FCSTD DOCUMENT
Label: Full set of dividers
objects: Sketcher::SketchObject×14
note: 14 computed .brp shape members not serialized (recipe doc carries the construction recipe); baked Part::Feature solids carry a one-line shape summary decoded from their .brp

FEATURE [Sketcher::SketchObject] Sketch  label="divider A000"
  sketch-geometry (20):
    g0: LineSegment StartX=0 StartY=31.25 StartZ=0 EndX=32 EndY=31.25 EndZ=0
    g1: LineSegment StartX=32 StartY=31.25 StartZ=0 EndX=32 EndY=15.625 EndZ=0
    g2: LineSegment StartX=32 StartY=15.625 StartZ=0 EndX=35 EndY=15.625 EndZ=0
    g3: LineSegment StartX=35 StartY=15.625 StartZ=0 EndX=35 EndY=31.25 EndZ=0
    g4: LineSegment StartX=35 StartY=31.25 StartZ=0 EndX=64 EndY=31.25 EndZ=0
    g5: LineSegment StartX=64 StartY=31.25 StartZ=0 EndX=64 EndY=15.625 EndZ=0
    g6: LineSegment StartX=64 StartY=15.625 StartZ=0 EndX=67 EndY=15.625 EndZ=0
    g7: LineSegment StartX=67 StartY=15.625 StartZ=0 EndX=67 EndY=31.25 EndZ=0
    g8: LineSegment StartX=67 StartY=31.25 StartZ=0 EndX=96 EndY=31.25 EndZ=0
    g9: LineSegment StartX=96 StartY=31.25 StartZ=0 EndX=96 EndY=15.625 EndZ=0
    g10: LineSegment StartX=96 StartY=15.625 StartZ=0 EndX=99 EndY=15.625 EndZ=0
    g11: LineSegment StartX=99 StartY=15.625 StartZ=0 EndX=99 EndY=31.25 EndZ=0
    g12: LineSegment StartX=99 StartY=31.25 StartZ=0 EndX=131 EndY=31.25 EndZ=0
    g13: LineSegment StartX=131 StartY=31.25 StartZ=0 EndX=131 EndY=15.625 EndZ=0
    g14: LineSegment StartX=131 StartY=15.625 StartZ=0 EndX=128 EndY=15.625 EndZ=0
    g15: LineSegment StartX=128 StartY=15.625 StartZ=0 EndX=128 EndY=0 EndZ=0
    g16: LineSegment StartX=128 StartY=0 StartZ=0 EndX=3 EndY=0 EndZ=0
    g17: LineSegment StartX=3 StartY=0 StartZ=0 EndX=3 EndY=15.625 EndZ=0
    g18: LineSegment StartX=3 StartY=15.625 StartZ=0 EndX=0 EndY=15.625 EndZ=0
    g19: LineSegment StartX=0 StartY=15.625 StartZ=0 EndX=0 EndY=31.25 EndZ=0
  constraints (60):
    c: Horizontal(g0)
    c: Coincident(g0,g1)
    c: Vertical(g1)
    c: Coincident(g1,g2)
    c: Horizontal(g2)
    c: Coincident(g2,g3)
    c: Coincident(g3,g4)
    c: Horizontal(g4)
    c: Coincident(g4,g5)
    c: Coincident(g5,g6)
    c: Horizontal(g6)
    c: Coincident(g6,g7)
    c: Coincident(g7,g8)
    c: Coincident(g8,g9)
    c: Vertical(g9)
    c: Coincident(g9,g10)
    c: Coincident(g10,g11)
    c: Vertical(g11)
    c: Coincident(g11,g12)
    c: Horizontal(g12)
    c: Coincident(g12,g13)
    c: Vertical(g13)
    c: Coincident(g13,g14)
    c: Coincident(g14,g15)
    c: Vertical(g15)
    c: Coincident(g15,g16)
    c: Horizontal(g16)
    c: Coincident(g16,g17)
    c: Vertical(g17)
    c: Coincident(g17,g18)
    c: Coincident(g18,g19)
    c: Coincident(g19,g0)
    c: Horizontal(g10)
    c: Horizontal(g14)
    c: Horizontal(g18)
    c: Vertical(g19)
    c: Vertical(g3)
    c: Vertical(g5)
    c: Vertical(g7)
    c: Horizontal(g8)
    c: DistanceY(g0,g3) = 0
    c: DistanceY(g4,g7) = 0
    c: DistanceY(g8,g11) = 0
    c: DistanceY(g6,g9) = 0
    c: DistanceY(g5,g2) = 0
    c: DistanceX(g1,g2) = 3
    c: DistanceX(g5,g6) = 3
    c: DistanceX(g8,g11) = 3
    c: DistanceY(g15,g12) = 31.25
    c: DistanceY(g13,g12) = 15.625
    c: DistanceY(g10,g14) = 0
    c: DistanceY(g17,g1) = 0
    c: DistanceX(g13,g14) = -3
    c: DistanceX(g18,g17) = 3
    c: DistanceX(g12,g11) = -32
    c: DistanceX(g4,g3) = -29
    c: DistanceX(g0,g0) = -32
    c: DistanceX(g7,g8) = 29
    c: DistanceX(g16) = 3
    c: DistanceY(g16) = 0
FEATURE [Sketcher::SketchObject] Sketch001  label="divider A001"
  Placement = pos=(0,62.5,0) rot=(1,0,0;3.14159rad)
  sketch-geometry (16):
    g0: LineSegment StartX=32 StartY=31.25 StartZ=0 EndX=32 EndY=15.625 EndZ=0
    g1: LineSegment StartX=32 StartY=15.625 StartZ=0 EndX=35 EndY=15.625 EndZ=0
    g2: LineSegment StartX=35 StartY=15.625 StartZ=0 EndX=35 EndY=31.25 EndZ=0
    g3: LineSegment StartX=64 StartY=31.25 StartZ=0 EndX=64 EndY=15.625 EndZ=0
    g4: LineSegment StartX=64 StartY=15.625 StartZ=0 EndX=67 EndY=15.625 EndZ=0
    g5: LineSegment StartX=67 StartY=15.625 StartZ=0 EndX=67 EndY=31.25 EndZ=0
    g6: LineSegment StartX=96 StartY=31.25 StartZ=0 EndX=96 EndY=15.625 EndZ=0
    g7: LineSegment StartX=96 StartY=15.625 StartZ=0 EndX=99 EndY=15.625 EndZ=0
    g8: LineSegment StartX=99 StartY=15.625 StartZ=0 EndX=99 EndY=31.25 EndZ=0
    g9: LineSegment StartX=131 StartY=31.25 StartZ=0 EndX=131 EndY=15.625 EndZ=0
    g10: LineSegment StartX=131 StartY=15.625 StartZ=0 EndX=128 EndY=15.625 EndZ=0
    g11: LineSegment StartX=128 StartY=15.625 StartZ=0 EndX=128 EndY=0 EndZ=0
    g12: LineSegment StartX=128 StartY=0 StartZ=0 EndX=3 EndY=0 EndZ=0
    g13: LineSegment StartX=3 StartY=0 StartZ=0 EndX=3 EndY=15.625 EndZ=0
    g14: LineSegment StartX=3 StartY=15.625 StartZ=0 EndX=0 EndY=15.625 EndZ=0
    g15: LineSegment StartX=0 StartY=15.625 StartZ=0 EndX=0 EndY=31.25 EndZ=0
  constraints (38):
    c: Vertical(g0)
    c: Coincident(g0,g1)
    c: Horizontal(g1)
    c: Coincident(g1,g2)
    c: Coincident(g3,g4)
    c: Horizontal(g4)
    c: Coincident(g4,g5)
    c: Vertical(g6)
    c: Coincident(g6,g7)
    c: Coincident(g7,g8)
    c: Vertical(g8)
    c: Vertical(g9)
    c: Coincident(g9,g10)
    c: Coincident(g10,g11)
    c: Vertical(g11)
    c: Coincident(g11,g12)
    c: Horizontal(g12)
    c: Coincident(g12,g13)
    c: Vertical(g13)
    c: Coincident(g13,g14)
    c: Coincident(g14,g15)
    c: Horizontal(g7)
    c: Horizontal(g10)
    c: Horizontal(g14)
    c: Vertical(g15)
    c: Vertical(g2)
    c: Vertical(g3)
    c: Vertical(g5)
    c: DistanceY(g4,g6) = 0
    c: DistanceY(g3,g1) = 0
    c: DistanceX(g0,g1) = 3
    c: DistanceX(g3,g4) = 3
    c: DistanceY(g7,g10) = 0
    c: DistanceY(g13,g0) = 0
    c: DistanceX(g9,g10) = -3
    c: DistanceX(g14,g13) = 3
    c: DistanceX(g12) = 3
    c: DistanceY(g12) = 0
FEATURE [Sketcher::SketchObject] Sketch002  label="divider A002"
  Placement = pos=(0,62.5,0) rot=(0,0,1;0rad)
  sketch-geometry (19):
    g0: LineSegment StartX=0 StartY=31.25 StartZ=0 EndX=32 EndY=31.25 EndZ=0
    g1: LineSegment StartX=32 StartY=31.25 StartZ=0 EndX=32 EndY=15.625 EndZ=0
    g2: LineSegment StartX=32 StartY=15.625 StartZ=0 EndX=35 EndY=15.625 EndZ=0
    g3: LineSegment StartX=35 StartY=15.625 StartZ=0 EndX=35 EndY=31.25 EndZ=0
    g4: LineSegment StartX=35 StartY=31.25 StartZ=0 EndX=64 EndY=31.25 EndZ=0
    g5: LineSegment StartX=64 StartY=31.25 StartZ=0 EndX=64 EndY=15.625 EndZ=0
    g6: LineSegment StartX=64 StartY=15.625 StartZ=0 EndX=67 EndY=15.625 EndZ=0
    g7: LineSegment StartX=67 StartY=15.625 StartZ=0 EndX=67 EndY=31.25 EndZ=0
    g8: LineSegment StartX=67 StartY=31.25 StartZ=0 EndX=96 EndY=31.25 EndZ=0
    g9: LineSegment StartX=96 StartY=31.25 StartZ=0 EndX=96 EndY=15.625 EndZ=0
    g10: LineSegment StartX=96 StartY=15.625 StartZ=0 EndX=99 EndY=15.625 EndZ=0
    g11: LineSegment StartX=99 StartY=15.625 StartZ=0 EndX=99 EndY=31.25 EndZ=0
    g12: LineSegment StartX=99 StartY=31.25 StartZ=0 EndX=131 EndY=31.25 EndZ=0
    g13: LineSegment StartX=131 StartY=31.25 StartZ=0 EndX=131 EndY=15.625 EndZ=0
    g14: LineSegment StartX=131 StartY=15.625 StartZ=0 EndX=128 EndY=15.625 EndZ=0
    g15: LineSegment StartX=128 StartY=15.625 StartZ=0 EndX=128 EndY=0 EndZ=0
    g16: LineSegment StartX=3 StartY=0 StartZ=0 EndX=3 EndY=15.625 EndZ=0
    g17: LineSegment StartX=3 StartY=15.625 StartZ=0 EndX=0 EndY=15.625 EndZ=0
    g18: LineSegment StartX=0 StartY=15.625 StartZ=0 EndX=0 EndY=31.25 EndZ=0
  constraints (55):
    c: Horizontal(g0)
    c: Coincident(g0,g1)
    c: Vertical(g1)
    c: Coincident(g1,g2)
    c: Horizontal(g2)
    c: Coincident(g2,g3)
    c: Coincident(g3,g4)
    c: Horizontal(g4)
    c: Coincident(g4,g5)
    c: Coincident(g5,g6)
    c: Horizontal(g6)
    c: Coincident(g6,g7)
    c: Coincident(g7,g8)
    c: Coincident(g8,g9)
    c: Vertical(g9)
    c: Coincident(g9,g10)
    c: Coincident(g10,g11)
    c: Vertical(g11)
    c: Coincident(g11,g12)
    c: Horizontal(g12)
    c: Coincident(g12,g13)
    c: Vertical(g13)
    c: Coincident(g13,g14)
    c: Coincident(g14,g15)
    c: Vertical(g15)
    c: Vertical(g16)
    c: Coincident(g16,g17)
    c: Coincident(g17,g18)
    c: Coincident(g18,g0)
    c: Horizontal(g10)
    c: Horizontal(g14)
    c: Horizontal(g17)
    c: Vertical(g18)
    c: Vertical(g3)
    c: Vertical(g5)
    c: Vertical(g7)
    c: Horizontal(g8)
    c: DistanceY(g0,g3) = 0
    c: DistanceY(g4,g7) = 0
    c: DistanceY(g8,g11) = 0
    c: DistanceY(g6,g9) = 0
    c: DistanceY(g5,g2) = 0
    c: DistanceX(g1,g2) = 3
    c: DistanceX(g5,g6) = 3
    c: DistanceX(g8,g11) = 3
    c: DistanceY(g15,g12) = 31.25
    c: DistanceY(g13,g12) = 15.625
    c: DistanceY(g10,g14) = 0
    c: DistanceY(g16,g1) = 0
    c: DistanceX(g13,g14) = -3
    c: DistanceX(g17,g16) = 3
    c: DistanceX(g12,g11) = -32
    c: DistanceX(g4,g3) = -29
    c: DistanceX(g0,g0) = -32
    c: DistanceX(g7,g8) = 29
FEATURE [Sketcher::SketchObject] Sketch003  label="divider A003"
  Placement = pos=(0,125,0) rot=(1,0,0;3.14159rad)
  sketch-geometry (16):
    g0: LineSegment StartX=32 StartY=31.25 StartZ=0 EndX=32 EndY=15.625 EndZ=0
    g1: LineSegment StartX=32 StartY=15.625 StartZ=0 EndX=35 EndY=15.625 EndZ=0
    g2: LineSegment StartX=35 StartY=15.625 StartZ=0 EndX=35 EndY=31.25 EndZ=0
    g3: LineSegment StartX=64 StartY=31.25 StartZ=0 EndX=64 EndY=15.625 EndZ=0
    g4: LineSegment StartX=64 StartY=15.625 StartZ=0 EndX=67 EndY=15.625 EndZ=0
    g5: LineSegment StartX=67 StartY=15.625 StartZ=0 EndX=67 EndY=31.25 EndZ=0
    g6: LineSegment StartX=96 StartY=31.25 StartZ=0 EndX=96 EndY=15.625 EndZ=0
    g7: LineSegment StartX=96 StartY=15.625 StartZ=0 EndX=99 EndY=15.625 EndZ=0
    g8: LineSegment StartX=99 StartY=15.625 StartZ=0 EndX=99 EndY=31.25 EndZ=0
    g9: LineSegment StartX=131 StartY=31.25 StartZ=0 EndX=131 EndY=15.625 EndZ=0
    g10: LineSegment StartX=131 StartY=15.625 StartZ=0 EndX=128 EndY=15.625 EndZ=0
    g11: LineSegment StartX=128 StartY=15.625 StartZ=0 EndX=128 EndY=0 EndZ=0
    g12: LineSegment StartX=128 StartY=0 StartZ=0 EndX=3 EndY=0 EndZ=0
    g13: LineSegment StartX=3 StartY=0 StartZ=0 EndX=3 EndY=15.625 EndZ=0
    g14: LineSegment StartX=3 StartY=15.625 StartZ=0 EndX=0 EndY=15.625 EndZ=0
    g15: LineSegment StartX=0 StartY=15.625 StartZ=0 EndX=0 EndY=31.25 EndZ=0
  constraints (38):
    c: Vertical(g0)
    c: Coincident(g0,g1)
    c: Horizontal(g1)
    c: Coincident(g1,g2)
    c: Coincident(g3,g4)
    c: Horizontal(g4)
    c: Coincident(g4,g5)
    c: Vertical(g6)
    c: Coincident(g6,g7)
    c: Coincident(g7,g8)
    c: Vertical(g8)
    c: Vertical(g9)
    c: Coincident(g9,g10)
    c: Coincident(g10,g11)
    c: Vertical(g11)
    c: Coincident(g11,g12)
    c: Horizontal(g12)
    c: Coincident(g12,g13)
    c: Vertical(g13)
    c: Coincident(g13,g14)
    c: Coincident(g14,g15)
    c: Horizontal(g7)
    c: Horizontal(g10)
    c: Horizontal(g14)
    c: Vertical(g15)
    c: Vertical(g2)
    c: Vertical(g3)
    c: Vertical(g5)
    c: DistanceY(g4,g6) = 0
    c: DistanceY(g3,g1) = 0
    c: DistanceX(g0,g1) = 3
    c: DistanceX(g3,g4) = 3
    c: DistanceY(g7,g10) = 0
    c: DistanceY(g13,g0) = 0
    c: DistanceX(g9,g10) = -3
    c: DistanceX(g14,g13) = 3
    c: DistanceX(g12) = 3
    c: DistanceY(g12) = 0
FEATURE [Sketcher::SketchObject] Sketch004  label="divider B000"
  Placement = pos=(128,0,0) rot=(0,0,1;0rad)
  sketch-geometry (17):
    g0: LineSegment StartX=3 StartY=31.25 StartZ=0 EndX=32 EndY=31.25 EndZ=0
    g1: LineSegment StartX=32 StartY=31.25 StartZ=0 EndX=32 EndY=15.625 EndZ=0
    g2: LineSegment StartX=32 StartY=15.625 StartZ=0 EndX=35 EndY=15.625 EndZ=0
    g3: LineSegment StartX=35 StartY=15.625 StartZ=0 EndX=35 EndY=31.25 EndZ=0
    g4: LineSegment StartX=35 StartY=31.25 StartZ=0 EndX=64 EndY=31.25 EndZ=0
    g5: LineSegment StartX=64 StartY=31.25 StartZ=0 EndX=64 EndY=15.625 EndZ=0
    g6: LineSegment StartX=64 StartY=15.625 StartZ=0 EndX=67 EndY=15.625 EndZ=0
    g7: LineSegment StartX=67 StartY=15.625 StartZ=0 EndX=67 EndY=31.25 EndZ=0
    g8: LineSegment StartX=67 StartY=31.25 StartZ=0 EndX=96 EndY=31.25 EndZ=0
    g9: LineSegment StartX=96 StartY=31.25 StartZ=0 EndX=96 EndY=15.625 EndZ=0
    g10: LineSegment StartX=96 StartY=15.625 StartZ=0 EndX=99 EndY=15.625 EndZ=0
    g11: LineSegment StartX=99 StartY=15.625 StartZ=0 EndX=99 EndY=31.25 EndZ=0
    g12: LineSegment StartX=99 StartY=31.25 StartZ=0 EndX=128 EndY=31.25 EndZ=0
    g13: LineSegment StartX=128 StartY=31.25 StartZ=0 EndX=128 EndY=15.625 EndZ=0
    g14: LineSegment StartX=128 StartY=15.625 StartZ=0 EndX=131 EndY=15.625 EndZ=0
    g15: LineSegment StartX=131 StartY=15.625 StartZ=0 EndX=131 EndY=0 EndZ=0
    g16: LineSegment StartX=131 StartY=0 StartZ=0 EndX=0 EndY=0 EndZ=0
  constraints (51):
    c: Horizontal(g0)
    c: Coincident(g0,g1)
    c: Vertical(g1)
    c: Coincident(g1,g2)
    c: Horizontal(g2)
    c: Coincident(g2,g3)
    c: Coincident(g3,g4)
    c: Horizontal(g4)
    c: Coincident(g4,g5)
    c: Coincident(g5,g6)
    c: Horizontal(g6)
    c: Coincident(g6,g7)
    c: Coincident(g7,g8)
    c: Coincident(g8,g9)
    c: Vertical(g9)
    c: Coincident(g9,g10)
    c: Coincident(g10,g11)
    c: Vertical(g11)
    c: Coincident(g11,g12)
    c: Horizontal(g12)
    c: Coincident(g12,g13)
    c: Vertical(g13)
    c: Coincident(g13,g14)
    c: Coincident(g14,g15)
    c: Vertical(g15)
    c: Coincident(g15,g16)
    c: Horizontal(g16)
    c: Horizontal(g10)
    c: Horizontal(g14)
    c: Vertical(g3)
    c: Vertical(g5)
    c: Vertical(g7)
    c: Horizontal(g8)
    c: DistanceY(g0,g3) = 0
    c: DistanceY(g4,g7) = 0
    c: DistanceY(g8,g11) = 0
    c: DistanceY(g6,g9) = 0
    c: DistanceY(g5,g2) = 0
    c: DistanceX(g1,g2) = 3
    c: DistanceX(g5,g6) = 3
    c: DistanceX(g8,g11) = 3
    c: DistanceY(g15,g12) = 31.25
    c: DistanceY(g13,g12) = 15.625
    c: DistanceY(g10,g14) = 0
    c: DistanceX(g13,g14) = 3
    c: DistanceX(g12,g11) = -29
    c: DistanceX(g4,g3) = -29
    c: DistanceX(g0,g0) = -29
    c: DistanceX(g7,g8) = 29
    c: DistanceX(g16) = 0
    c: DistanceY(g16) = 0
FEATURE [Sketcher::SketchObject] Sketch005  label="divider B001"
  Placement = pos=(128,62.5,0) rot=(1,0,0;3.14159rad)
  sketch-geometry (14):
    g0: LineSegment StartX=32 StartY=31.25 StartZ=0 EndX=32 EndY=15.625 EndZ=0
    g1: LineSegment StartX=32 StartY=15.625 StartZ=0 EndX=35 EndY=15.625 EndZ=0
    g2: LineSegment StartX=35 StartY=15.625 StartZ=0 EndX=35 EndY=31.25 EndZ=0
    g3: LineSegment StartX=64 StartY=31.25 StartZ=0 EndX=64 EndY=15.625 EndZ=0
    g4: LineSegment StartX=64 StartY=15.625 StartZ=0 EndX=67 EndY=15.625 EndZ=0
    g5: LineSegment StartX=67 StartY=15.625 StartZ=0 EndX=67 EndY=31.25 EndZ=0
    g6: LineSegment StartX=96 StartY=31.25 StartZ=0 EndX=96 EndY=15.625 EndZ=0
    g7: LineSegment StartX=96 StartY=15.625 StartZ=0 EndX=99 EndY=15.625 EndZ=0
    g8: LineSegment StartX=99 StartY=15.625 StartZ=0 EndX=99 EndY=31.25 EndZ=0
    g9: LineSegment StartX=99 StartY=31.25 StartZ=0 EndX=128 EndY=31.25 EndZ=0
    g10: LineSegment StartX=128 StartY=31.25 StartZ=0 EndX=128 EndY=15.625 EndZ=0
    g11: LineSegment StartX=128 StartY=15.625 StartZ=0 EndX=131 EndY=15.625 EndZ=0
    g12: LineSegment StartX=131 StartY=15.625 StartZ=0 EndX=131 EndY=0 EndZ=0
    g13: LineSegment StartX=131 StartY=0 StartZ=0 EndX=0 EndY=0 EndZ=0
  constraints (36):
    c: Vertical(g0)
    c: Coincident(g0,g1)
    c: Horizontal(g1)
    c: Coincident(g1,g2)
    c: Coincident(g3,g4)
    c: Horizontal(g4)
    c: Coincident(g4,g5)
    c: Vertical(g6)
    c: Coincident(g6,g7)
    c: Coincident(g7,g8)
    c: Vertical(g8)
    c: Coincident(g8,g9)
    c: Horizontal(g9)
    c: Coincident(g9,g10)
    c: Vertical(g10)
    c: Coincident(g10,g11)
    c: Coincident(g11,g12)
    c: Vertical(g12)
    c: Coincident(g12,g13)
    c: Horizontal(g13)
    c: Horizontal(g7)
    c: Horizontal(g11)
    c: Vertical(g2)
    c: Vertical(g3)
    c: Vertical(g5)
    c: DistanceY(g4,g6) = 0
    c: DistanceY(g3,g1) = 0
    c: DistanceX(g0,g1) = 3
    c: DistanceX(g3,g4) = 3
    c: DistanceY(g12,g9) = 31.25
    c: DistanceY(g10,g9) = 15.625
    c: DistanceY(g7,g11) = 0
    c: DistanceX(g10,g11) = 3
    c: DistanceX(g9,g8) = -29
    c: DistanceX(g13) = 0
    c: DistanceY(g13) = 0
FEATURE [Sketcher::SketchObject] Sketch006  label="divider B002"
  Placement = pos=(128,62.5,0) rot=(0,0,1;0rad)
  sketch-geometry (13):
    g0: LineSegment StartX=32 StartY=31.25 StartZ=0 EndX=32 EndY=15.625 EndZ=0
    g1: LineSegment StartX=32 StartY=15.625 StartZ=0 EndX=35 EndY=15.625 EndZ=0
    g2: LineSegment StartX=35 StartY=15.625 StartZ=0 EndX=35 EndY=31.25 EndZ=0
    g3: LineSegment StartX=64 StartY=31.25 StartZ=0 EndX=64 EndY=15.625 EndZ=0
    g4: LineSegment StartX=64 StartY=15.625 StartZ=0 EndX=67 EndY=15.625 EndZ=0
    g5: LineSegment StartX=67 StartY=15.625 StartZ=0 EndX=67 EndY=31.25 EndZ=0
    g6: LineSegment StartX=96 StartY=31.25 StartZ=0 EndX=96 EndY=15.625 EndZ=0
    g7: LineSegment StartX=96 StartY=15.625 StartZ=0 EndX=99 EndY=15.625 EndZ=0
    g8: LineSegment StartX=99 StartY=15.625 StartZ=0 EndX=99 EndY=31.25 EndZ=0
    g9: LineSegment StartX=99 StartY=31.25 StartZ=0 EndX=128 EndY=31.25 EndZ=0
    g10: LineSegment StartX=128 StartY=31.25 StartZ=0 EndX=128 EndY=15.625 EndZ=0
    g11: LineSegment StartX=128 StartY=15.625 StartZ=0 EndX=131 EndY=15.625 EndZ=0
    g12: LineSegment StartX=131 StartY=15.625 StartZ=0 EndX=131 EndY=0 EndZ=0
  constraints (32):
    c: Vertical(g0)
    c: Coincident(g0,g1)
    c: Horizontal(g1)
    c: Coincident(g1,g2)
    c: Coincident(g3,g4)
    c: Horizontal(g4)
    c: Coincident(g4,g5)
    c: Vertical(g6)
    c: Coincident(g6,g7)
    c: Coincident(g7,g8)
    c: Vertical(g8)
    c: Coincident(g8,g9)
    c: Horizontal(g9)
    c: Coincident(g9,g10)
    c: Vertical(g10)
    c: Coincident(g10,g11)
    c: Coincident(g11,g12)
    c: Vertical(g12)
    c: Horizontal(g7)
    c: Horizontal(g11)
    c: Vertical(g2)
    c: Vertical(g3)
    c: Vertical(g5)
    c: DistanceY(g4,g6) = 0
    c: DistanceY(g3,g1) = 0
    c: DistanceX(g0,g1) = 3
    c: DistanceX(g3,g4) = 3
    c: DistanceY(g12,g9) = 31.25
    c: DistanceY(g10,g9) = 15.625
    c: DistanceY(g7,g11) = 0
    c: DistanceX(g10,g11) = 3
    c: DistanceX(g9,g8) = -29
FEATURE [Sketcher::SketchObject] Sketch007  label="divider A"
  Placement = pos=(128,93.75,0) rot=(0,0,1;0rad)
  sketch-geometry (14):
    g0: LineSegment StartX=32 StartY=31.25 StartZ=0 EndX=32 EndY=15.625 EndZ=0
    g1: LineSegment StartX=32 StartY=15.625 StartZ=0 EndX=35 EndY=15.625 EndZ=0
    g2: LineSegment StartX=35 StartY=15.625 StartZ=0 EndX=35 EndY=31.25 EndZ=0
    g3: LineSegment StartX=64 StartY=31.25 StartZ=0 EndX=64 EndY=15.625 EndZ=0
    g4: LineSegment StartX=64 StartY=15.625 StartZ=0 EndX=67 EndY=15.625 EndZ=0
    g5: LineSegment StartX=67 StartY=15.625 StartZ=0 EndX=67 EndY=31.25 EndZ=0
    g6: LineSegment StartX=96 StartY=31.25 StartZ=0 EndX=96 EndY=15.625 EndZ=0
    g7: LineSegment StartX=96 StartY=15.625 StartZ=0 EndX=99 EndY=15.625 EndZ=0
    g8: LineSegment StartX=99 StartY=15.625 StartZ=0 EndX=99 EndY=31.25 EndZ=0
    g9: LineSegment StartX=99 StartY=31.25 StartZ=0 EndX=131 EndY=31.25 EndZ=0
    g10: LineSegment StartX=131 StartY=31.25 StartZ=0 EndX=131 EndY=15.625 EndZ=0
    g11: LineSegment StartX=131 StartY=15.625 StartZ=0 EndX=128 EndY=15.625 EndZ=0
    g12: LineSegment StartX=128 StartY=15.625 StartZ=0 EndX=128 EndY=0 EndZ=0
    g13: LineSegment StartX=128 StartY=0 StartZ=0 EndX=3 EndY=0 EndZ=0
  constraints (36):
    c: Vertical(g0)
    c: Coincident(g0,g1)
    c: Horizontal(g1)
    c: Coincident(g1,g2)
    c: Coincident(g3,g4)
    c: Horizontal(g4)
    c: Coincident(g4,g5)
    c: Vertical(g6)
    c: Coincident(g6,g7)
    c: Coincident(g7,g8)
    c: Vertical(g8)
    c: Coincident(g8,g9)
    c: Horizontal(g9)
    c: Coincident(g9,g10)
    c: Vertical(g10)
    c: Coincident(g10,g11)
    c: Coincident(g11,g12)
    c: Vertical(g12)
    c: Coincident(g12,g13)
    c: Horizontal(g13)
    c: Horizontal(g7)
    c: Horizontal(g11)
    c: Vertical(g2)
    c: Vertical(g3)
    c: Vertical(g5)
    c: DistanceY(g4,g6) = 0
    c: DistanceY(g3,g1) = 0
    c: DistanceX(g0,g1) = 3
    c: DistanceX(g3,g4) = 3
    c: DistanceY(g12,g9) = 31.25
    c: DistanceY(g10,g9) = 15.625
    c: DistanceY(g7,g11) = 0
    c: DistanceX(g10,g11) = -3
    c: DistanceX(g9,g8) = -32
    c: DistanceX(g13) = 3
    c: DistanceY(g13) = 0
FEATURE [Sketcher::SketchObject] Sketch008  label="divider A004"
  Placement = pos=(128,156.25,0) rot=(1,0,0;3.14159rad)
  sketch-geometry (20):
    g0: LineSegment StartX=0 StartY=31.25 StartZ=0 EndX=32 EndY=31.25 EndZ=0
    g1: LineSegment StartX=32 StartY=31.25 StartZ=0 EndX=32 EndY=15.625 EndZ=0
    g2: LineSegment StartX=32 StartY=15.625 StartZ=0 EndX=35 EndY=15.625 EndZ=0
    g3: LineSegment StartX=35 StartY=15.625 StartZ=0 EndX=35 EndY=31.25 EndZ=0
    g4: LineSegment StartX=35 StartY=31.25 StartZ=0 EndX=64 EndY=31.25 EndZ=0
    g5: LineSegment StartX=64 StartY=31.25 StartZ=0 EndX=64 EndY=15.625 EndZ=0
    g6: LineSegment StartX=64 StartY=15.625 StartZ=0 EndX=67 EndY=15.625 EndZ=0
    g7: LineSegment StartX=67 StartY=15.625 StartZ=0 EndX=67 EndY=31.25 EndZ=0
    g8: LineSegment StartX=67 StartY=31.25 StartZ=0 EndX=96 EndY=31.25 EndZ=0
    g9: LineSegment StartX=96 StartY=31.25 StartZ=0 EndX=96 EndY=15.625 EndZ=0
    g10: LineSegment StartX=96 StartY=15.625 StartZ=0 EndX=99 EndY=15.625 EndZ=0
    g11: LineSegment StartX=99 StartY=15.625 StartZ=0 EndX=99 EndY=31.25 EndZ=0
    g12: LineSegment StartX=99 StartY=31.25 StartZ=0 EndX=131 EndY=31.25 EndZ=0
    g13: LineSegment StartX=131 StartY=31.25 StartZ=0 EndX=131 EndY=15.625 EndZ=0
    g14: LineSegment StartX=131 StartY=15.625 StartZ=0 EndX=128 EndY=15.625 EndZ=0
    g15: LineSegment StartX=128 StartY=15.625 StartZ=0 EndX=128 EndY=0 EndZ=0
    g16: LineSegment StartX=128 StartY=0 StartZ=0 EndX=3 EndY=0 EndZ=0
    g17: LineSegment StartX=3 StartY=0 StartZ=0 EndX=3 EndY=15.625 EndZ=0
    g18: LineSegment StartX=3 StartY=15.625 StartZ=0 EndX=0 EndY=15.625 EndZ=0
    g19: LineSegment StartX=0 StartY=15.625 StartZ=0 EndX=0 EndY=31.25 EndZ=0
  constraints (60):
    c: Horizontal(g0)
    c: Coincident(g0,g1)
    c: Vertical(g1)
    c: Coincident(g1,g2)
    c: Horizontal(g2)
    c: Coincident(g2,g3)
    c: Coincident(g3,g4)
    c: Horizontal(g4)
    c: Coincident(g4,g5)
    c: Coincident(g5,g6)
    c: Horizontal(g6)
    c: Coincident(g6,g7)
    c: Coincident(g7,g8)
    c: Coincident(g8,g9)
    c: Vertical(g9)
    c: Coincident(g9,g10)
    c: Coincident(g10,g11)
    c: Vertical(g11)
    c: Coincident(g11,g12)
    c: Horizontal(g12)
    c: Coincident(g12,g13)
    c: Vertical(g13)
    c: Coincident(g13,g14)
    c: Coincident(g14,g15)
    c: Vertical(g15)
    c: Coincident(g15,g16)
    c: Horizontal(g16)
    c: Coincident(g16,g17)
    c: Vertical(g17)
    c: Coincident(g17,g18)
    c: Coincident(g18,g19)
    c: Coincident(g19,g0)
    c: Horizontal(g10)
    c: Horizontal(g14)
    c: Horizontal(g18)
    c: Vertical(g19)
    c: Vertical(g3)
    c: Vertical(g5)
    c: Vertical(g7)
    c: Horizontal(g8)
    c: DistanceY(g0,g3) = 0
    c: DistanceY(g4,g7) = 0
    c: DistanceY(g8,g11) = 0
    c: DistanceY(g6,g9) = 0
    c: DistanceY(g5,g2) = 0
    c: DistanceX(g1,g2) = 3
    c: DistanceX(g5,g6) = 3
    c: DistanceX(g8,g11) = 3
    c: DistanceY(g15,g12) = 31.25
    c: DistanceY(g13,g12) = 15.625
    c: DistanceY(g10,g14) = 0
    c: DistanceY(g17,g1) = 0
    c: DistanceX(g13,g14) = -3
    c: DistanceX(g18,g17) = 3
    c: DistanceX(g12,g11) = -32
    c: DistanceX(g4,g3) = -29
    c: DistanceX(g0,g0) = -32
    c: DistanceX(g7,g8) = 29
    c: DistanceX(g16) = 3
    c: DistanceY(g16) = 0
FEATURE [Sketcher::SketchObject] Sketch009  label="divider B"
  Placement = pos=(0,156.25,0) rot=(1,0,0;3.14159rad)
  sketch-geometry (13):
    g0: LineSegment StartX=32 StartY=31.25 StartZ=0 EndX=32 EndY=15.625 EndZ=0
    g1: LineSegment StartX=32 StartY=15.625 StartZ=0 EndX=35 EndY=15.625 EndZ=0
    g2: LineSegment StartX=35 StartY=15.625 StartZ=0 EndX=35 EndY=31.25 EndZ=0
    g3: LineSegment StartX=64 StartY=31.25 StartZ=0 EndX=64 EndY=15.625 EndZ=0
    g4: LineSegment StartX=64 StartY=15.625 StartZ=0 EndX=67 EndY=15.625 EndZ=0
    g5: LineSegment StartX=67 StartY=15.625 StartZ=0 EndX=67 EndY=31.25 EndZ=0
    g6: LineSegment StartX=96 StartY=31.25 StartZ=0 EndX=96 EndY=15.625 EndZ=0
    g7: LineSegment StartX=96 StartY=15.625 StartZ=0 EndX=99 EndY=15.625 EndZ=0
    g8: LineSegment StartX=99 StartY=15.625 StartZ=0 EndX=99 EndY=31.25 EndZ=0
    g9: LineSegment StartX=131 StartY=0 StartZ=0 EndX=0 EndY=0 EndZ=0
    g10: LineSegment StartX=0 StartY=0 StartZ=0 EndX=0 EndY=15.625 EndZ=0
    g11: LineSegment StartX=0 StartY=15.625 StartZ=0 EndX=3 EndY=15.625 EndZ=0
    g12: LineSegment StartX=3 StartY=15.625 StartZ=0 EndX=3 EndY=31.25 EndZ=0
  constraints (30):
    c: Vertical(g0)
    c: Coincident(g0,g1)
    c: Horizontal(g1)
    c: Coincident(g1,g2)
    c: Coincident(g3,g4)
    c: Horizontal(g4)
    c: Coincident(g4,g5)
    c: Vertical(g6)
    c: Coincident(g6,g7)
    c: Coincident(g7,g8)
    c: Vertical(g8)
    c: Horizontal(g9)
    c: Coincident(g9,g10)
    c: Vertical(g10)
    c: Coincident(g10,g11)
    c: Coincident(g11,g12)
    c: Horizontal(g7)
    c: Horizontal(g11)
    c: Vertical(g12)
    c: Vertical(g2)
    c: Vertical(g3)
    c: Vertical(g5)
    c: DistanceY(g4,g6) = 0
    c: DistanceY(g3,g1) = 0
    c: DistanceX(g0,g1) = 3
    c: DistanceX(g3,g4) = 3
    c: DistanceY(g10,g0) = 0
    c: DistanceX(g11,g10) = -3
    c: DistanceX(g9) = 0
    c: DistanceY(g9) = 0
FEATURE [Sketcher::SketchObject] Sketch010  label="divider B003"
  Placement = pos=(0,156.25,0) rot=(0,0,1;0rad)
  sketch-geometry (19):
    g0: LineSegment StartX=3 StartY=31.25 StartZ=0 EndX=32 EndY=31.25 EndZ=0
    g1: LineSegment StartX=32 StartY=31.25 StartZ=0 EndX=32 EndY=15.625 EndZ=0
    g2: LineSegment StartX=32 StartY=15.625 StartZ=0 EndX=35 EndY=15.625 EndZ=0
    g3: LineSegment StartX=35 StartY=15.625 StartZ=0 EndX=35 EndY=31.25 EndZ=0
    g4: LineSegment StartX=35 StartY=31.25 StartZ=0 EndX=64 EndY=31.25 EndZ=0
    g5: LineSegment StartX=64 StartY=31.25 StartZ=0 EndX=64 EndY=15.625 EndZ=0
    g6: LineSegment StartX=64 StartY=15.625 StartZ=0 EndX=67 EndY=15.625 EndZ=0
    g7: LineSegment StartX=67 StartY=15.625 StartZ=0 EndX=67 EndY=31.25 EndZ=0
    g8: LineSegment StartX=67 StartY=31.25 StartZ=0 EndX=96 EndY=31.25 EndZ=0
    g9: LineSegment StartX=96 StartY=31.25 StartZ=0 EndX=96 EndY=15.625 EndZ=0
    g10: LineSegment StartX=96 StartY=15.625 StartZ=0 EndX=99 EndY=15.625 EndZ=0
    g11: LineSegment StartX=99 StartY=15.625 StartZ=0 EndX=99 EndY=31.25 EndZ=0
    g12: LineSegment StartX=99 StartY=31.25 StartZ=0 EndX=128 EndY=31.25 EndZ=0
    g13: LineSegment StartX=128 StartY=31.25 StartZ=0 EndX=128 EndY=15.625 EndZ=0
    g14: LineSegment StartX=128 StartY=15.625 StartZ=0 EndX=131 EndY=15.625 EndZ=0
    g15: LineSegment StartX=131 StartY=15.625 StartZ=0 EndX=131 EndY=0 EndZ=0
    g16: LineSegment StartX=0 StartY=0 StartZ=0 EndX=0 EndY=15.625 EndZ=0
    g17: LineSegment StartX=0 StartY=15.625 StartZ=0 EndX=3 EndY=15.625 EndZ=0
    g18: LineSegment StartX=3 StartY=15.625 StartZ=0 EndX=3 EndY=31.25 EndZ=0
  constraints (55):
    c: Horizontal(g0)
    c: Coincident(g0,g1)
    c: Vertical(g1)
    c: Coincident(g1,g2)
    c: Horizontal(g2)
    c: Coincident(g2,g3)
    c: Coincident(g3,g4)
    c: Horizontal(g4)
    c: Coincident(g4,g5)
    c: Coincident(g5,g6)
    c: Horizontal(g6)
    c: Coincident(g6,g7)
    c: Coincident(g7,g8)
    c: Coincident(g8,g9)
    c: Vertical(g9)
    c: Coincident(g9,g10)
    c: Coincident(g10,g11)
    c: Vertical(g11)
    c: Coincident(g11,g12)
    c: Horizontal(g12)
    c: Coincident(g12,g13)
    c: Vertical(g13)
    c: Coincident(g13,g14)
    c: Coincident(g14,g15)
    c: Vertical(g15)
    c: Vertical(g16)
    c: Coincident(g16,g17)
    c: Coincident(g17,g18)
    c: Coincident(g18,g0)
    c: Horizontal(g10)
    c: Horizontal(g14)
    c: Horizontal(g17)
    c: Vertical(g18)
    c: Vertical(g3)
    c: Vertical(g5)
    c: Vertical(g7)
    c: Horizontal(g8)
    c: DistanceY(g0,g3) = 0
    c: DistanceY(g4,g7) = 0
    c: DistanceY(g8,g11) = 0
    c: DistanceY(g6,g9) = 0
    c: DistanceY(g5,g2) = 0
    c: DistanceX(g1,g2) = 3
    c: DistanceX(g5,g6) = 3
    c: DistanceX(g8,g11) = 3
    c: DistanceY(g15,g12) = 31.25
    c: DistanceY(g13,g12) = 15.625
    c: DistanceY(g10,g14) = 0
    c: DistanceY(g16,g1) = 0
    c: DistanceX(g13,g14) = 3
    c: DistanceX(g17,g16) = -3
    c: DistanceX(g12,g11) = -29
    c: DistanceX(g4,g3) = -29
    c: DistanceX(g0,g0) = -29
    c: DistanceX(g7,g8) = 29
FEATURE [Sketcher::SketchObject] Sketch011  label="divider A005"
  Placement = pos=(128,156.25,0) rot=(0,0,1;0rad)
  sketch-geometry (16):
    g0: LineSegment StartX=0 StartY=31.25 StartZ=0 EndX=32 EndY=31.25 EndZ=0
    g1: LineSegment StartX=32 StartY=31.25 StartZ=0 EndX=32 EndY=15.625 EndZ=0
    g2: LineSegment StartX=32 StartY=15.625 StartZ=0 EndX=35 EndY=15.625 EndZ=0
    g3: LineSegment StartX=35 StartY=15.625 StartZ=0 EndX=35 EndY=31.25 EndZ=0
    g4: LineSegment StartX=35 StartY=31.25 StartZ=0 EndX=64 EndY=31.25 EndZ=0
    g5: LineSegment StartX=64 StartY=31.25 StartZ=0 EndX=64 EndY=15.625 EndZ=0
    g6: LineSegment StartX=64 StartY=15.625 StartZ=0 EndX=67 EndY=15.625 EndZ=0
    g7: LineSegment StartX=67 StartY=15.625 StartZ=0 EndX=67 EndY=31.25 EndZ=0
    g8: LineSegment StartX=67 StartY=31.25 StartZ=0 EndX=96 EndY=31.25 EndZ=0
    g9: LineSegment StartX=96 StartY=15.625 StartZ=0 EndX=99 EndY=15.625 EndZ=0
    g10: LineSegment StartX=99 StartY=15.625 StartZ=0 EndX=99 EndY=31.25 EndZ=0
    g11: LineSegment StartX=99 StartY=31.25 StartZ=0 EndX=131 EndY=31.25 EndZ=0
    g12: LineSegment StartX=131 StartY=31.25 StartZ=0 EndX=131 EndY=15.625 EndZ=0
    g13: LineSegment StartX=131 StartY=15.625 StartZ=0 EndX=128 EndY=15.625 EndZ=0
    g14: LineSegment StartX=128 StartY=15.625 StartZ=0 EndX=128 EndY=0 EndZ=0
    g15: LineSegment StartX=96 StartY=15.625 StartZ=0 EndX=96 EndY=31.25 EndZ=0
  constraints (48):
    c: Horizontal(g0)
    c: Coincident(g0,g1)
    c: Vertical(g1)
    c: Coincident(g1,g2)
    c: Horizontal(g2)
    c: Coincident(g2,g3)
    c: Coincident(g3,g4)
    c: Horizontal(g4)
    c: Coincident(g4,g5)
    c: Coincident(g5,g6)
    c: Horizontal(g6)
    c: Coincident(g6,g7)
    c: Coincident(g7,g8)
    c: Coincident(g9,g10)
    c: Vertical(g10)
    c: Coincident(g10,g11)
    c: Horizontal(g11)
    c: Coincident(g11,g12)
    c: Vertical(g12)
    c: Coincident(g12,g13)
    c: Coincident(g13,g14)
    c: Vertical(g14)
    c: Horizontal(g9)
    c: Horizontal(g13)
    c: Vertical(g3)
    c: Vertical(g5)
    c: Vertical(g7)
    c: Horizontal(g8)
    c: DistanceY(g0,g3) = 0
    c: DistanceY(g4,g7) = 0
    c: DistanceY(g8,g10) = 0
    c: DistanceY(g5,g2) = 0
    c: DistanceX(g1,g2) = 3
    c: DistanceX(g5,g6) = 3
    c: DistanceX(g8,g10) = 3
    c: DistanceY(g14,g11) = 31.25
    c: DistanceY(g12,g11) = 15.625
    c: DistanceY(g9,g13) = 0
    c: DistanceX(g12,g13) = -3
    c: DistanceX(g11,g10) = -32
    c: DistanceX(g4,g3) = -29
    c: DistanceX(g0,g0) = -32
    c: DistanceX(g7,g8) = 29
    c: Coincident(g15,g8)
    c: Coincident(g15,g9)
    c: Vertical(g15)
    c: DistanceX(g14) = 128
    c: DistanceY(g14) = 0
FEATURE [Sketcher::SketchObject] Sketch012  label="divider A006"
  Placement = pos=(128,218.75,0) rot=(1,0,0;3.14159rad)
  sketch-geometry (16):
    g0: LineSegment StartX=32 StartY=31.25 StartZ=0 EndX=32 EndY=15.625 EndZ=0
    g1: LineSegment StartX=32 StartY=15.625 StartZ=0 EndX=35 EndY=15.625 EndZ=0
    g2: LineSegment StartX=35 StartY=15.625 StartZ=0 EndX=35 EndY=31.25 EndZ=0
    g3: LineSegment StartX=64 StartY=31.25 StartZ=0 EndX=64 EndY=15.625 EndZ=0
    g4: LineSegment StartX=64 StartY=15.625 StartZ=0 EndX=67 EndY=15.625 EndZ=0
    g5: LineSegment StartX=67 StartY=15.625 StartZ=0 EndX=67 EndY=31.25 EndZ=0
    g6: LineSegment StartX=96 StartY=31.25 StartZ=0 EndX=96 EndY=15.625 EndZ=0
    g7: LineSegment StartX=96 StartY=15.625 StartZ=0 EndX=99 EndY=15.625 EndZ=0
    g8: LineSegment StartX=99 StartY=15.625 StartZ=0 EndX=99 EndY=31.25 EndZ=0
    g9: LineSegment StartX=131 StartY=31.25 StartZ=0 EndX=131 EndY=15.625 EndZ=0
    g10: LineSegment StartX=131 StartY=15.625 StartZ=0 EndX=128 EndY=15.625 EndZ=0
    g11: LineSegment StartX=128 StartY=15.625 StartZ=0 EndX=128 EndY=0 EndZ=0
    g12: LineSegment StartX=128 StartY=0 StartZ=0 EndX=3 EndY=0 EndZ=0
    g13: LineSegment StartX=3 StartY=0 StartZ=0 EndX=3 EndY=15.625 EndZ=0
    g14: LineSegment StartX=3 StartY=15.625 StartZ=0 EndX=0 EndY=15.625 EndZ=0
    g15: LineSegment StartX=0 StartY=15.625 StartZ=0 EndX=0 EndY=31.25 EndZ=0
  constraints (38):
    c: Vertical(g0)
    c: Coincident(g0,g1)
    c: Horizontal(g1)
    c: Coincident(g1,g2)
    c: Coincident(g3,g4)
    c: Horizontal(g4)
    c: Coincident(g4,g5)
    c: Vertical(g6)
    c: Coincident(g6,g7)
    c: Coincident(g7,g8)
    c: Vertical(g8)
    c: Vertical(g9)
    c: Coincident(g9,g10)
    c: Coincident(g10,g11)
    c: Vertical(g11)
    c: Coincident(g11,g12)
    c: Horizontal(g12)
    c: Coincident(g12,g13)
    c: Vertical(g13)
    c: Coincident(g13,g14)
    c: Coincident(g14,g15)
    c: Horizontal(g7)
    c: Horizontal(g10)
    c: Horizontal(g14)
    c: Vertical(g15)
    c: Vertical(g2)
    c: Vertical(g3)
    c: Vertical(g5)
    c: DistanceY(g4,g6) = 0
    c: DistanceY(g3,g1) = 0
    c: DistanceX(g0,g1) = 3
    c: DistanceX(g3,g4) = 3
    c: DistanceY(g7,g10) = 0
    c: DistanceY(g13,g0) = 0
    c: DistanceX(g9,g10) = -3
    c: DistanceX(g14,g13) = 3
    c: DistanceX(g12) = 3
    c: DistanceY(g12) = 0
FEATURE [Sketcher::SketchObject] Sketch013  label="divider B004"
  Placement = pos=(0,218.75,0) rot=(1,0,0;3.14159rad)
  sketch-geometry (13):
    g0: LineSegment StartX=32 StartY=31.25 StartZ=0 EndX=32 EndY=15.625 EndZ=0
    g1: LineSegment StartX=32 StartY=15.625 StartZ=0 EndX=35 EndY=15.625 EndZ=0
    g2: LineSegment StartX=35 StartY=15.625 StartZ=0 EndX=35 EndY=31.25 EndZ=0
    g3: LineSegment StartX=64 StartY=31.25 StartZ=0 EndX=64 EndY=15.625 EndZ=0
    g4: LineSegment StartX=64 StartY=15.625 StartZ=0 EndX=67 EndY=15.625 EndZ=0
    g5: LineSegment StartX=67 StartY=15.625 StartZ=0 EndX=67 EndY=31.25 EndZ=0
    g6: LineSegment StartX=96 StartY=31.25 StartZ=0 EndX=96 EndY=15.625 EndZ=0
    g7: LineSegment StartX=96 StartY=15.625 StartZ=0 EndX=99 EndY=15.625 EndZ=0
    g8: LineSegment StartX=99 StartY=15.625 StartZ=0 EndX=99 EndY=31.25 EndZ=0
    g9: LineSegment StartX=131 StartY=0 StartZ=0 EndX=0 EndY=0 EndZ=0
    g10: LineSegment StartX=0 StartY=0 StartZ=0 EndX=0 EndY=15.625 EndZ=0
    g11: LineSegment StartX=0 StartY=15.625 StartZ=0 EndX=3 EndY=15.625 EndZ=0
    g12: LineSegment StartX=3 StartY=15.625 StartZ=0 EndX=3 EndY=31.25 EndZ=0
  constraints (30):
    c: Vertical(g0)
    c: Coincident(g0,g1)
    c: Horizontal(g1)
    c: Coincident(g1,g2)
    c: Coincident(g3,g4)
    c: Horizontal(g4)
    c: Coincident(g4,g5)
    c: Vertical(g6)
    c: Coincident(g6,g7)
    c: Coincident(g7,g8)
    c: Vertical(g8)
    c: Horizontal(g9)
    c: Coincident(g9,g10)
    c: Vertical(g10)
    c: Coincident(g10,g11)
    c: Coincident(g11,g12)
    c: Horizontal(g7)
    c: Horizontal(g11)
    c: Vertical(g12)
    c: Vertical(g2)
    c: Vertical(g3)
    c: Vertical(g5)
    c: DistanceY(g4,g6) = 0
    c: DistanceY(g3,g1) = 0
    c: DistanceX(g0,g1) = 3
    c: DistanceX(g3,g4) = 3
    c: DistanceY(g10,g0) = 0
    c: DistanceX(g11,g10) = -3
    c: DistanceX(g9) = 0
    c: DistanceY(g9) = 0
